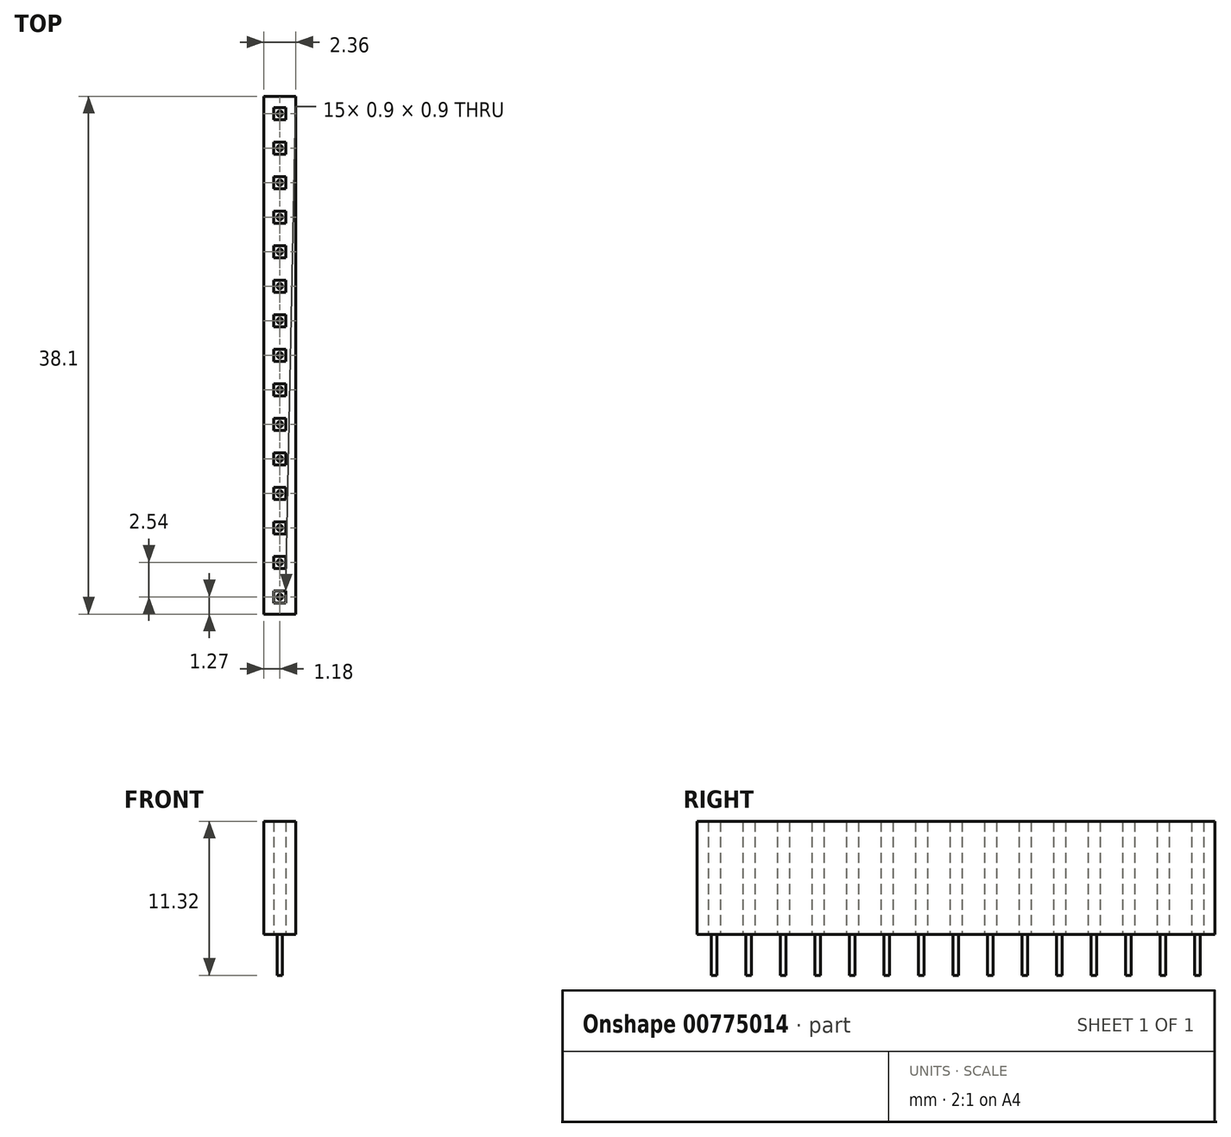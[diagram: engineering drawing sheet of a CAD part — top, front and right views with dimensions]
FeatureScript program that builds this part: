
annotation { "Feature Type Name" : "Feature", "Feature Type Description" : "" }
export const myFeature = defineFeature(function(context is Context, id is Id, definition is map)
    precondition{}
    {
        {
            var Q0;
            Q0=qCreatedBy(makeId("Top.planeOp"),FACE);
            var sketch = newSketch(context, id + "F0", { "sketchPlane" : qUnion([Q0])});
            skLineSegment(sketch, "E0.bottom", {"start": v(-1.17, 0) * mm, "end": v(1.17, 0) * mm});
            skLineSegment(sketch, "E0.top", {"start": v(-1.18, -38.1) * mm, "end": v(1.18, -38.1) * mm});
            skLineSegment(sketch, "E0.left", {"start": v(-1.17, 0) * mm, "end": v(-1.17, -38.1) * mm});
            skLineSegment(sketch, "E0.right", {"start": v(1.18, 0) * mm, "end": v(1.18, -38.1) * mm});
            skLineSegment(sketch, "E1.bottom", {"start": v(-0.45, -0.82) * mm, "end": v(0.45, -0.82) * mm});
            skLineSegment(sketch, "E1.top", {"start": v(-0.45, -1.72) * mm, "end": v(0.45, -1.72) * mm});
            skLineSegment(sketch, "E1.left", {"start": v(-0.45, -0.82) * mm, "end": v(-0.45, -1.72) * mm});
            skLineSegment(sketch, "E1.right", {"start": v(0.45, -0.82) * mm, "end": v(0.45, -1.72) * mm});
            skLineSegment(sketch, "E2.1.0.0", {"start": v(-0.45, -3.36) * mm, "end": v(0.45, -3.36) * mm});
            skLineSegment(sketch, "E2.1.0.1", {"start": v(0.45, -3.36) * mm, "end": v(0.45, -4.26) * mm});
            skLineSegment(sketch, "E2.1.0.2", {"start": v(-0.45, -4.26) * mm, "end": v(0.45, -4.26) * mm});
            skLineSegment(sketch, "E2.1.0.3", {"start": v(-0.45, -3.36) * mm, "end": v(-0.45, -4.26) * mm});
            skLineSegment(sketch, "E2.2.0.0", {"start": v(-0.45, -5.9) * mm, "end": v(0.45, -5.9) * mm});
            skLineSegment(sketch, "E2.2.0.1", {"start": v(0.45, -5.9) * mm, "end": v(0.45, -6.8) * mm});
            skLineSegment(sketch, "E2.2.0.2", {"start": v(-0.45, -6.8) * mm, "end": v(0.45, -6.8) * mm});
            skLineSegment(sketch, "E2.2.0.3", {"start": v(-0.45, -5.9) * mm, "end": v(-0.45, -6.8) * mm});
            skLineSegment(sketch, "E2.3.0.0", {"start": v(-0.45, -8.44) * mm, "end": v(0.45, -8.44) * mm});
            skLineSegment(sketch, "E2.3.0.1", {"start": v(0.45, -8.44) * mm, "end": v(0.45, -9.34) * mm});
            skLineSegment(sketch, "E2.3.0.2", {"start": v(-0.45, -9.34) * mm, "end": v(0.45, -9.34) * mm});
            skLineSegment(sketch, "E2.3.0.3", {"start": v(-0.45, -8.44) * mm, "end": v(-0.45, -9.34) * mm});
            skLineSegment(sketch, "E2.4.0.0", {"start": v(-0.45, -10.98) * mm, "end": v(0.45, -10.98) * mm});
            skLineSegment(sketch, "E2.4.0.1", {"start": v(0.45, -10.98) * mm, "end": v(0.45, -11.88) * mm});
            skLineSegment(sketch, "E2.4.0.2", {"start": v(-0.45, -11.88) * mm, "end": v(0.45, -11.88) * mm});
            skLineSegment(sketch, "E2.4.0.3", {"start": v(-0.45, -10.98) * mm, "end": v(-0.45, -11.88) * mm});
            skLineSegment(sketch, "E2.5.0.0", {"start": v(-0.45, -13.52) * mm, "end": v(0.45, -13.52) * mm});
            skLineSegment(sketch, "E2.5.0.1", {"start": v(0.45, -13.52) * mm, "end": v(0.45, -14.42) * mm});
            skLineSegment(sketch, "E2.5.0.2", {"start": v(-0.45, -14.42) * mm, "end": v(0.45, -14.42) * mm});
            skLineSegment(sketch, "E2.5.0.3", {"start": v(-0.45, -13.52) * mm, "end": v(-0.45, -14.42) * mm});
            skLineSegment(sketch, "E2.6.0.0", {"start": v(-0.45, -16.06) * mm, "end": v(0.45, -16.06) * mm});
            skLineSegment(sketch, "E2.6.0.1", {"start": v(0.45, -16.06) * mm, "end": v(0.45, -16.96) * mm});
            skLineSegment(sketch, "E2.6.0.2", {"start": v(-0.45, -16.96) * mm, "end": v(0.45, -16.96) * mm});
            skLineSegment(sketch, "E2.6.0.3", {"start": v(-0.45, -16.06) * mm, "end": v(-0.45, -16.96) * mm});
            skLineSegment(sketch, "E2.7.0.0", {"start": v(-0.45, -18.6) * mm, "end": v(0.45, -18.6) * mm});
            skLineSegment(sketch, "E2.7.0.1", {"start": v(0.45, -18.6) * mm, "end": v(0.45, -19.5) * mm});
            skLineSegment(sketch, "E2.7.0.2", {"start": v(-0.45, -19.5) * mm, "end": v(0.45, -19.5) * mm});
            skLineSegment(sketch, "E2.7.0.3", {"start": v(-0.45, -18.6) * mm, "end": v(-0.45, -19.5) * mm});
            skLineSegment(sketch, "E2.8.0.0", {"start": v(-0.45, -21.14) * mm, "end": v(0.45, -21.14) * mm});
            skLineSegment(sketch, "E2.8.0.1", {"start": v(0.45, -21.14) * mm, "end": v(0.45, -22.04) * mm});
            skLineSegment(sketch, "E2.8.0.2", {"start": v(-0.45, -22.04) * mm, "end": v(0.45, -22.04) * mm});
            skLineSegment(sketch, "E2.8.0.3", {"start": v(-0.45, -21.14) * mm, "end": v(-0.45, -22.04) * mm});
            skLineSegment(sketch, "E2.9.0.0", {"start": v(-0.45, -23.68) * mm, "end": v(0.45, -23.68) * mm});
            skLineSegment(sketch, "E2.9.0.1", {"start": v(0.45, -23.68) * mm, "end": v(0.45, -24.58) * mm});
            skLineSegment(sketch, "E2.9.0.2", {"start": v(-0.45, -24.58) * mm, "end": v(0.45, -24.58) * mm});
            skLineSegment(sketch, "E2.9.0.3", {"start": v(-0.45, -23.68) * mm, "end": v(-0.45, -24.58) * mm});
            skLineSegment(sketch, "E2.10.0.0", {"start": v(-0.45, -26.22) * mm, "end": v(0.45, -26.22) * mm});
            skLineSegment(sketch, "E2.10.0.1", {"start": v(0.45, -26.22) * mm, "end": v(0.45, -27.12) * mm});
            skLineSegment(sketch, "E2.10.0.2", {"start": v(-0.45, -27.12) * mm, "end": v(0.45, -27.12) * mm});
            skLineSegment(sketch, "E2.10.0.3", {"start": v(-0.45, -26.22) * mm, "end": v(-0.45, -27.12) * mm});
            skLineSegment(sketch, "E2.11.0.0", {"start": v(-0.45, -28.76) * mm, "end": v(0.45, -28.76) * mm});
            skLineSegment(sketch, "E2.11.0.1", {"start": v(0.45, -28.76) * mm, "end": v(0.45, -29.66) * mm});
            skLineSegment(sketch, "E2.11.0.2", {"start": v(-0.45, -29.66) * mm, "end": v(0.45, -29.66) * mm});
            skLineSegment(sketch, "E2.11.0.3", {"start": v(-0.45, -28.76) * mm, "end": v(-0.45, -29.66) * mm});
            skLineSegment(sketch, "E2.12.0.0", {"start": v(-0.45, -31.3) * mm, "end": v(0.45, -31.3) * mm});
            skLineSegment(sketch, "E2.12.0.1", {"start": v(0.45, -31.3) * mm, "end": v(0.45, -32.2) * mm});
            skLineSegment(sketch, "E2.12.0.2", {"start": v(-0.45, -32.2) * mm, "end": v(0.45, -32.2) * mm});
            skLineSegment(sketch, "E2.12.0.3", {"start": v(-0.45, -31.3) * mm, "end": v(-0.45, -32.2) * mm});
            skLineSegment(sketch, "E2.13.0.0", {"start": v(-0.45, -33.84) * mm, "end": v(0.45, -33.84) * mm});
            skLineSegment(sketch, "E2.13.0.1", {"start": v(0.45, -33.84) * mm, "end": v(0.45, -34.74) * mm});
            skLineSegment(sketch, "E2.13.0.2", {"start": v(-0.45, -34.74) * mm, "end": v(0.45, -34.74) * mm});
            skLineSegment(sketch, "E2.13.0.3", {"start": v(-0.45, -33.84) * mm, "end": v(-0.45, -34.74) * mm});
            skLineSegment(sketch, "E2.14.0.0", {"start": v(-0.45, -36.38) * mm, "end": v(0.45, -36.38) * mm});
            skLineSegment(sketch, "E2.14.0.1", {"start": v(0.45, -36.38) * mm, "end": v(0.45, -37.28) * mm});
            skLineSegment(sketch, "E2.14.0.2", {"start": v(-0.45, -37.28) * mm, "end": v(0.45, -37.28) * mm});
            skLineSegment(sketch, "E2.14.0.3", {"start": v(-0.45, -36.38) * mm, "end": v(-0.45, -37.28) * mm});
            skLineSegment(sketch, "E2.direction1", {"start": v(-0.45, -0.82) * mm, "end": v(-0.45, -3.36) * mm, "construction": true});
            skSolve(sketch);
        }
        {
            var Q0;
            Q0=makeQuery(id+"F0.imprint","IMPRINT",FACE,{"disambiguationData":[TD([[makeQuery(id+"F0.imprint","IMPRINT",EDGE,{"derivedFrom":sQuery(id+"F0.wireOp",EDGE,"E0.bottom")}),-1.0]])]});
            extrude(context, id + "F1", {"entities" : qUnion([Q0]), "depth" : 8.32 * mm, "offsetDistance" : 25 * mm});
        }
        {
            var Q0;
            Q0=makeQuery(id+"F1.opExtrude","CAP_FACE",FACE,{"disambiguationData":[OSD([sQuery(id+"F0.wireOp",EDGE,"E0.bottom"),sQuery(id+"F0.wireOp",EDGE,"E0.top"),sQuery(id+"F0.wireOp",EDGE,"E0.left"),sQuery(id+"F0.wireOp",EDGE,"E0.right"),sQuery(id+"F0.wireOp",EDGE,"E1.bottom"),sQuery(id+"F0.wireOp",EDGE,"E1.top"),sQuery(id+"F0.wireOp",EDGE,"E1.left"),sQuery(id+"F0.wireOp",EDGE,"E1.right"),sQuery(id+"F0.wireOp",EDGE,"E2.1.0.0"),sQuery(id+"F0.wireOp",EDGE,"E2.1.0.1"),sQuery(id+"F0.wireOp",EDGE,"E2.1.0.2"),sQuery(id+"F0.wireOp",EDGE,"E2.1.0.3"),sQuery(id+"F0.wireOp",EDGE,"E2.2.0.0"),sQuery(id+"F0.wireOp",EDGE,"E2.2.0.1"),sQuery(id+"F0.wireOp",EDGE,"E2.2.0.2"),sQuery(id+"F0.wireOp",EDGE,"E2.2.0.3"),sQuery(id+"F0.wireOp",EDGE,"E2.3.0.0"),sQuery(id+"F0.wireOp",EDGE,"E2.3.0.1"),sQuery(id+"F0.wireOp",EDGE,"E2.3.0.2"),sQuery(id+"F0.wireOp",EDGE,"E2.3.0.3"),sQuery(id+"F0.wireOp",EDGE,"E2.4.0.0"),sQuery(id+"F0.wireOp",EDGE,"E2.4.0.1"),sQuery(id+"F0.wireOp",EDGE,"E2.4.0.2"),sQuery(id+"F0.wireOp",EDGE,"E2.4.0.3"),sQuery(id+"F0.wireOp",EDGE,"E2.5.0.0"),sQuery(id+"F0.wireOp",EDGE,"E2.5.0.1"),sQuery(id+"F0.wireOp",EDGE,"E2.5.0.2"),sQuery(id+"F0.wireOp",EDGE,"E2.5.0.3"),sQuery(id+"F0.wireOp",EDGE,"E2.6.0.0"),sQuery(id+"F0.wireOp",EDGE,"E2.6.0.1"),sQuery(id+"F0.wireOp",EDGE,"E2.6.0.2"),sQuery(id+"F0.wireOp",EDGE,"E2.6.0.3"),sQuery(id+"F0.wireOp",EDGE,"E2.7.0.0"),sQuery(id+"F0.wireOp",EDGE,"E2.7.0.1"),sQuery(id+"F0.wireOp",EDGE,"E2.7.0.2"),sQuery(id+"F0.wireOp",EDGE,"E2.7.0.3"),sQuery(id+"F0.wireOp",EDGE,"E2.8.0.0"),sQuery(id+"F0.wireOp",EDGE,"E2.8.0.1"),sQuery(id+"F0.wireOp",EDGE,"E2.8.0.2"),sQuery(id+"F0.wireOp",EDGE,"E2.8.0.3"),sQuery(id+"F0.wireOp",EDGE,"E2.9.0.0"),sQuery(id+"F0.wireOp",EDGE,"E2.9.0.1"),sQuery(id+"F0.wireOp",EDGE,"E2.9.0.2"),sQuery(id+"F0.wireOp",EDGE,"E2.9.0.3"),sQuery(id+"F0.wireOp",EDGE,"E2.10.0.0"),sQuery(id+"F0.wireOp",EDGE,"E2.10.0.1"),sQuery(id+"F0.wireOp",EDGE,"E2.10.0.2"),sQuery(id+"F0.wireOp",EDGE,"E2.10.0.3"),sQuery(id+"F0.wireOp",EDGE,"E2.11.0.0"),sQuery(id+"F0.wireOp",EDGE,"E2.11.0.1"),sQuery(id+"F0.wireOp",EDGE,"E2.11.0.2"),sQuery(id+"F0.wireOp",EDGE,"E2.11.0.3"),sQuery(id+"F0.wireOp",EDGE,"E2.12.0.0"),sQuery(id+"F0.wireOp",EDGE,"E2.12.0.1"),sQuery(id+"F0.wireOp",EDGE,"E2.12.0.2"),sQuery(id+"F0.wireOp",EDGE,"E2.12.0.3"),sQuery(id+"F0.wireOp",EDGE,"E2.13.0.0"),sQuery(id+"F0.wireOp",EDGE,"E2.13.0.1"),sQuery(id+"F0.wireOp",EDGE,"E2.13.0.2"),sQuery(id+"F0.wireOp",EDGE,"E2.13.0.3"),sQuery(id+"F0.wireOp",EDGE,"E2.14.0.0"),sQuery(id+"F0.wireOp",EDGE,"E2.14.0.1"),sQuery(id+"F0.wireOp",EDGE,"E2.14.0.2"),sQuery(id+"F0.wireOp",EDGE,"E2.14.0.3")])],"isStart":true});
            var sketch = newSketch(context, id + "F2", { "sketchPlane" : qUnion([Q0])});
            skCircle(sketch, "E3", {"center": v(0, 36.83) * mm, "radius": 0.2 * mm});
            skCircle(sketch, "E4.1.0.0", {"center": v(0, 34.3) * mm, "radius": 0.2 * mm});
            skCircle(sketch, "E4.2.0.0", {"center": v(0, 31.75) * mm, "radius": 0.2 * mm});
            skCircle(sketch, "E4.3.0.0", {"center": v(0, 29.21) * mm, "radius": 0.2 * mm});
            skCircle(sketch, "E4.4.0.0", {"center": v(0, 26.67) * mm, "radius": 0.2 * mm});
            skCircle(sketch, "E4.5.0.0", {"center": v(0, 24.13) * mm, "radius": 0.2 * mm});
            skCircle(sketch, "E4.6.0.0", {"center": v(0, 21.59) * mm, "radius": 0.2 * mm});
            skCircle(sketch, "E4.7.0.0", {"center": v(0, 19.05) * mm, "radius": 0.2 * mm});
            skCircle(sketch, "E4.8.0.0", {"center": v(0, 16.5) * mm, "radius": 0.2 * mm});
            skCircle(sketch, "E4.9.0.0", {"center": v(0, 13.97) * mm, "radius": 0.2 * mm});
            skCircle(sketch, "E4.10.0.0", {"center": v(0, 11.43) * mm, "radius": 0.2 * mm});
            skCircle(sketch, "E4.11.0.0", {"center": v(0, 8.89) * mm, "radius": 0.2 * mm});
            skCircle(sketch, "E4.12.0.0", {"center": v(0, 6.35) * mm, "radius": 0.2 * mm});
            skCircle(sketch, "E4.13.0.0", {"center": v(0, 3.8) * mm, "radius": 0.2 * mm});
            skCircle(sketch, "E4.14.0.0", {"center": v(0, 1.27) * mm, "radius": 0.2 * mm});
            skLineSegment(sketch, "E4.direction1", {"start": v(0, 36.83) * mm, "end": v(0, 34.3) * mm, "construction": true});
            skSolve(sketch);
        }
        {
            var Q0;
            Q0 = qSketchRegion(id + "F2", true);
            extrude(context, id + "F3", {"entities" : qUnion([Q0]), "depth" : 3 * mm, "offsetDistance" : 25 * mm});
        }
    });
